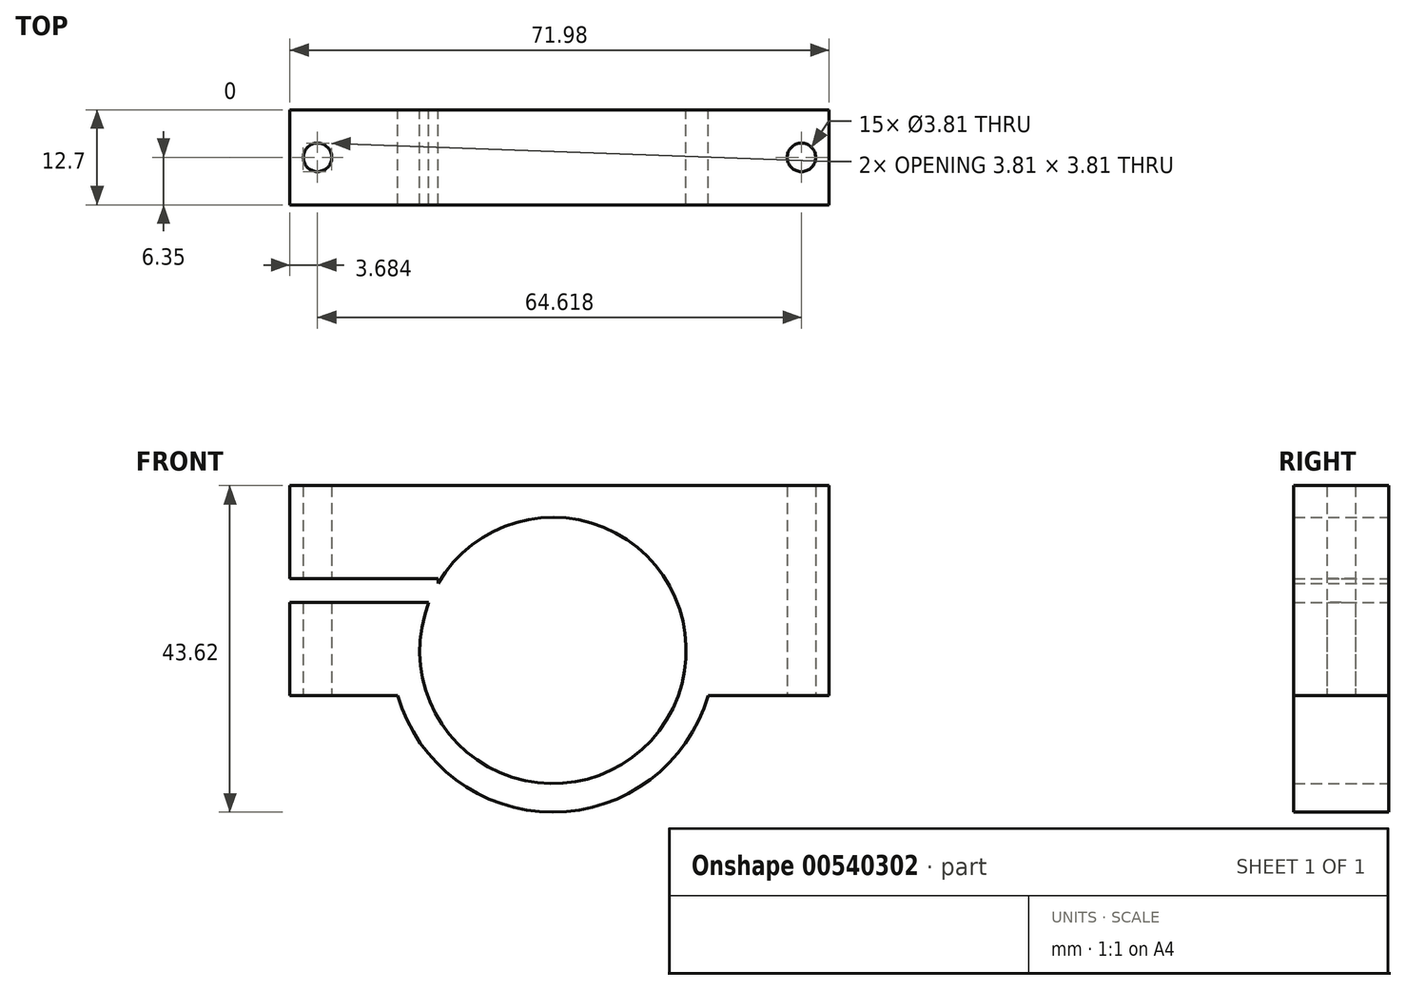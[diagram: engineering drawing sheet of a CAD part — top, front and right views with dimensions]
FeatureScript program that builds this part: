
annotation { "Feature Type Name" : "Feature", "Feature Type Description" : "" }
export const myFeature = defineFeature(function(context is Context, id is Id, definition is map)
    precondition{}
    {
        {
            var Q0;
            Q0=qCreatedBy(makeId("Front.planeOp"),FACE);
            var sketch = newSketch(context, id + "F0", { "sketchPlane" : qUnion([Q0])});
            skLineSegment(sketch, "E0.bottom", {"start": v(-0.6, 41.96) * mm, "end": v(-72.59, 41.96) * mm});
            skLineSegment(sketch, "E0.top", {"start": v(-0.6, 13.92) * mm, "end": v(-72.59, 13.92) * mm});
            skLineSegment(sketch, "E0.left", {"start": v(-0.6, 41.96) * mm, "end": v(-0.6, 13.92) * mm});
            skLineSegment(sketch, "E0.right", {"start": v(-72.59, 41.96) * mm, "end": v(-72.59, 13.92) * mm});
            skLineSegment(sketch, "E1.bottom", {"start": v(-59.5, 29.53) * mm, "end": v(-85.68, 29.53) * mm});
            skLineSegment(sketch, "E1.top", {"start": v(-59.5, 26.35) * mm, "end": v(-85.68, 26.35) * mm});
            skLineSegment(sketch, "E1.left", {"start": v(-59.5, 29.53) * mm, "end": v(-59.5, 26.35) * mm});
            skLineSegment(sketch, "E1.right", {"start": v(-85.68, 29.53) * mm, "end": v(-85.68, 26.35) * mm});
            skPoint(sketch, "E1.middle", {"position": v(-72.59, 27.94) * mm});
            skLineSegment(sketch, "E2.bottom", {"start": v(-59.5, 26.35) * mm, "end": v(-52.83, 26.35) * mm});
            skLineSegment(sketch, "E2.top", {"start": v(-59.5, 29.53) * mm, "end": v(-52.83, 29.53) * mm});
            skLineSegment(sketch, "E2.left", {"start": v(-59.5, 26.35) * mm, "end": v(-59.5, 29.53) * mm});
            skLineSegment(sketch, "E2.right", {"start": v(-52.83, 26.35) * mm, "end": v(-52.83, 29.53) * mm});
            skLineSegment(sketch, "E3.bottom", {"start": v(-72.59, 41.96) * mm, "end": v(-2.7, 41.96) * mm});
            skLineSegment(sketch, "E3.left", {"start": v(-72.59, 41.96) * mm, "end": v(-72.59, 46.21) * mm});
            skLineSegment(sketch, "E3.right", {"start": v(-2.7, 41.96) * mm, "end": v(-2.7, 46.21) * mm});
            skCircle(sketch, "E4", {"center": v(-37.47, 19.93) * mm, "radius": 21.59 * mm});
            skCircle(sketch, "E5", {"center": v(-37.47, 19.93) * mm, "radius": 17.78 * mm});
            skSolve(sketch);
        }
        {
            var Q0;
            Q0=makeQuery(id+"F0.imprint","IMPRINT",FACE,{"disambiguationData":[TD([[makeQuery(id+"F0.imprint","IMPRINT",EDGE,{"derivedFrom":sQuery(id+"F0.wireOp",EDGE,"E3.top")}),-1.0]])]});
            var Q1;
            {var subQ1=sQuery(id+"F0.wireOp",EDGE,"E0.right");var subQ3=sQuery(id+"F0.wireOp",EDGE,"E1.bottom");var subQ4=makeQuery(id+"F0.imprint","INTERSECT",VERTEX,{"derivedFrom":[subQ1,subQ3]});Q1=makeQuery(id+"F0.imprint","IMPRINT",FACE,{"disambiguationData":[TD([[makeQuery(id+"F0.imprint","IMPRINT",EDGE,{"disambiguationData":[TD([[subQ4,1.0]])],"derivedFrom":subQ1}),1.0]])]});}
            var Q2;
            {var subQ0=sQuery(id+"F0.wireOp",EDGE,"E0.right");var subQ1=sQuery(id+"F0.wireOp",EDGE,"E0.top");var subQ2=makeQuery(id+"F0.imprint","INTERSECT",VERTEX,{"derivedFrom":[subQ1,subQ0]});Q2=makeQuery(id+"F0.imprint","IMPRINT",FACE,{"disambiguationData":[TD([[makeQuery(id+"F0.imprint","IMPRINT",EDGE,{"disambiguationData":[TD([[subQ2,1.0]])],"derivedFrom":subQ1}),-1.0]])]});}
            var Q3;
            {var subQ0=sQuery(id+"F0.wireOp",EDGE,"sbxEEFek-9CQg-n1o7-jYzT-jlpCqLiAxBRQ");var subQ1=sQuery(id+"F0.wireOp",EDGE,"E0.top");var subQ2=makeQuery(id+"F0.imprint","INTERSECT",VERTEX,{"disambiguationData":[OD(0.0)],"derivedFrom":[subQ1,subQ0]});Q3=makeQuery(id+"F0.imprint","IMPRINT",FACE,{"disambiguationData":[TD([[makeQuery(id+"F0.imprint","IMPRINT",EDGE,{"disambiguationData":[TD([[subQ2,-1.0]])],"derivedFrom":subQ1}),1.0]])]});}
            var Q4;
            {var subQ3=sQuery(id+"F0.wireOp",EDGE,"sbxEEFek-9CQg-n1o7-jYzT-jlpCqLiAxBRQ");var subQ6=sQuery(id+"F0.wireOp",EDGE,"E0.top");var subQ9=makeQuery(id+"F0.imprint","INTERSECT",VERTEX,{"disambiguationData":[OD(1.0)],"derivedFrom":[subQ6,subQ3]});Q4=makeQuery(id+"F0.imprint","IMPRINT",FACE,{"disambiguationData":[TD([[makeQuery(id+"F0.imprint","IMPRINT",EDGE,{"disambiguationData":[TD([[subQ9,1.0]])],"derivedFrom":subQ6}),-1.0]])]});}
            var Q5;
            {var subQ0=sQuery(id+"F0.wireOp",EDGE,"sbxEEFek-9CQg-n1o7-jYzT-jlpCqLiAxBRQ");var subQ1=sQuery(id+"F0.wireOp",EDGE,"E0.top");var subQ2=makeQuery(id+"F0.imprint","INTERSECT",VERTEX,{"disambiguationData":[OD(0.0)],"derivedFrom":[subQ1,subQ0]});Q5=makeQuery(id+"F0.imprint","IMPRINT",FACE,{"disambiguationData":[TD([[makeQuery(id+"F0.imprint","IMPRINT",EDGE,{"disambiguationData":[TD([[subQ2,-1.0]])],"derivedFrom":subQ1}),-1.0]])]});}
            var Q6;
            {var subQ0=sQuery(id+"F0.wireOp",EDGE,"E0.left");Q6=makeQuery(id+"F0.imprint","IMPRINT",FACE,{"disambiguationData":[TD([[makeQuery(id+"F0.imprint","IMPRINT",EDGE,{"derivedFrom":subQ0}),-1.0]])]});}
            var Q7;
            {var subQ0=sQuery(id+"F0.wireOp",EDGE,"E4");var subQ1=sQuery(id+"F0.wireOp",EDGE,"E2.top");var subQ2=makeQuery(id+"F0.imprint","INTERSECT",VERTEX,{"derivedFrom":[subQ1,subQ0]});Q7=makeQuery(id+"F0.imprint","IMPRINT",FACE,{"disambiguationData":[TD([[makeQuery(id+"F0.imprint","IMPRINT",EDGE,{"disambiguationData":[TD([[subQ2,-1.0]])],"derivedFrom":subQ1}),1.0]])]});}
            var Q8;
            {var subQ0=sQuery(id+"F0.wireOp",EDGE,"E4");var subQ1=sQuery(id+"F0.wireOp",EDGE,"E0.top");var subQ2=makeQuery(id+"F0.imprint","INTERSECT",VERTEX,{"disambiguationData":[OD(0.0)],"derivedFrom":[subQ1,subQ0]});Q8=makeQuery(id+"F0.imprint","IMPRINT",FACE,{"disambiguationData":[TD([[makeQuery(id+"F0.imprint","IMPRINT",EDGE,{"disambiguationData":[TD([[subQ2,-1.0]])],"derivedFrom":subQ1}),1.0]])]});}
            var Q9;
            {var subQ0=sQuery(id+"F0.wireOp",EDGE,"E4");var subQ1=sQuery(id+"F0.wireOp",EDGE,"E0.top");var subQ2=makeQuery(id+"F0.imprint","INTERSECT",VERTEX,{"disambiguationData":[OD(1.0)],"derivedFrom":[subQ1,subQ0]});Q9=makeQuery(id+"F0.imprint","IMPRINT",FACE,{"disambiguationData":[TD([[makeQuery(id+"F0.imprint","IMPRINT",EDGE,{"disambiguationData":[TD([[subQ2,1.0]])],"derivedFrom":subQ1}),-1.0]])]});}
            var Q10;
            {var subQ0=sQuery(id+"F0.wireOp",EDGE,"E4");var subQ1=sQuery(id+"F0.wireOp",EDGE,"E0.top");var subQ2=makeQuery(id+"F0.imprint","INTERSECT",VERTEX,{"disambiguationData":[OD(0.0)],"derivedFrom":[subQ1,subQ0]});Q10=makeQuery(id+"F0.imprint","IMPRINT",FACE,{"disambiguationData":[TD([[makeQuery(id+"F0.imprint","IMPRINT",EDGE,{"disambiguationData":[TD([[subQ2,-1.0]])],"derivedFrom":subQ1}),-1.0]])]});}
            var Q11;
            {var subQ0=sQuery(id+"F0.wireOp",EDGE,"E4");var subQ1=sQuery(id+"F0.wireOp",EDGE,"E3.bottom");var subQ2=makeQuery(id+"F0.imprint","INTERSECT",VERTEX,{"disambiguationData":[OD(0.0)],"derivedFrom":[subQ1,subQ0]});Q11=makeQuery(id+"F0.imprint","IMPRINT",FACE,{"disambiguationData":[TD([[makeQuery(id+"F0.imprint","IMPRINT",EDGE,{"disambiguationData":[TD([[subQ2,-1.0]])],"derivedFrom":subQ1}),1.0]])]});}
            extrude(context, id + "F1", {"entities" : qUnion([Q0, Q1, Q2, Q3, Q4, Q5, Q6, Q7, Q8, Q9, Q10, Q11]), "depth" : 12.7 * mm, "offsetDistance" : 25.4 * mm});
        }
        {
            var Q0;
            Q0=qCreatedBy(makeId("Top.planeOp"),FACE);
            var sketch = newSketch(context, id + "F2", { "sketchPlane" : qUnion([Q0])});
            skCircle(sketch, "E6", {"center": v(-68.9, -6.35) * mm, "radius": 1.9 * mm});
            skCircle(sketch, "E7", {"center": v(-4.29, -6.35) * mm, "radius": 1.9 * mm});
            skPoint(sketch, "E8", {"position": v(-68.9, -8.26) * mm});
            skPoint(sketch, "E9", {"position": v(-67, -6.35) * mm});
            skPoint(sketch, "E10", {"position": v(-68.9, -4.44) * mm});
            skPoint(sketch, "E11", {"position": v(-70.81, -6.35) * mm});
            skPoint(sketch, "E12", {"position": v(-4.29, -4.44) * mm});
            skPoint(sketch, "E13", {"position": v(-4.29, -8.26) * mm});
            skPoint(sketch, "E14", {"position": v(-6.2, -6.35) * mm});
            skPoint(sketch, "E15", {"position": v(-2.38, -6.35) * mm});
            skSolve(sketch);
        }
        {
            var Q0;
            Q0=sQuery(id+"F2.wireOp",VERTEX,"E6.center");
            var Q1;
            Q1=sQuery(id+"F2.wireOp",VERTEX,"E7.center");
            var Q2;
            Q2=makeQuery(id+"F1.opExtrude","SWEPT_BODY",BODY,{"disambiguationData":[OSD([sQuery(id+"F0.wireOp",EDGE,"E0.bottom"),sQuery(id+"F0.wireOp",EDGE,"E0.top"),sQuery(id+"F0.wireOp",EDGE,"E0.left"),sQuery(id+"F0.wireOp",EDGE,"E0.right"),sQuery(id+"F0.wireOp",EDGE,"E1.bottom"),sQuery(id+"F0.wireOp",EDGE,"E1.top"),sQuery(id+"F0.wireOp",EDGE,"E2.bottom"),sQuery(id+"F0.wireOp",EDGE,"E2.top"),sQuery(id+"F0.wireOp",EDGE,"E2.right"),sQuery(id+"F0.wireOp",EDGE,"E3.bottom"),sQuery(id+"F0.wireOp",EDGE,"E4"),sQuery(id+"F0.wireOp",EDGE,"E5")])]});
            hole(context, id + "F3", {"style" : HoleStyle.SIMPLE, "endStyle" : HoleEndStyle.THROUGH, "oppositeDirection" : true, "holeDiameter" : 3.8 * mm, "majorDiameter" : 6.35 * mm, "isTappedThrough" : true, "tappedDepth" : 12.7 * mm, "tapClearance" : 3, "locations" : qUnion([Q0, Q1]), "scope" : qUnion([Q2])});
        }
    });
